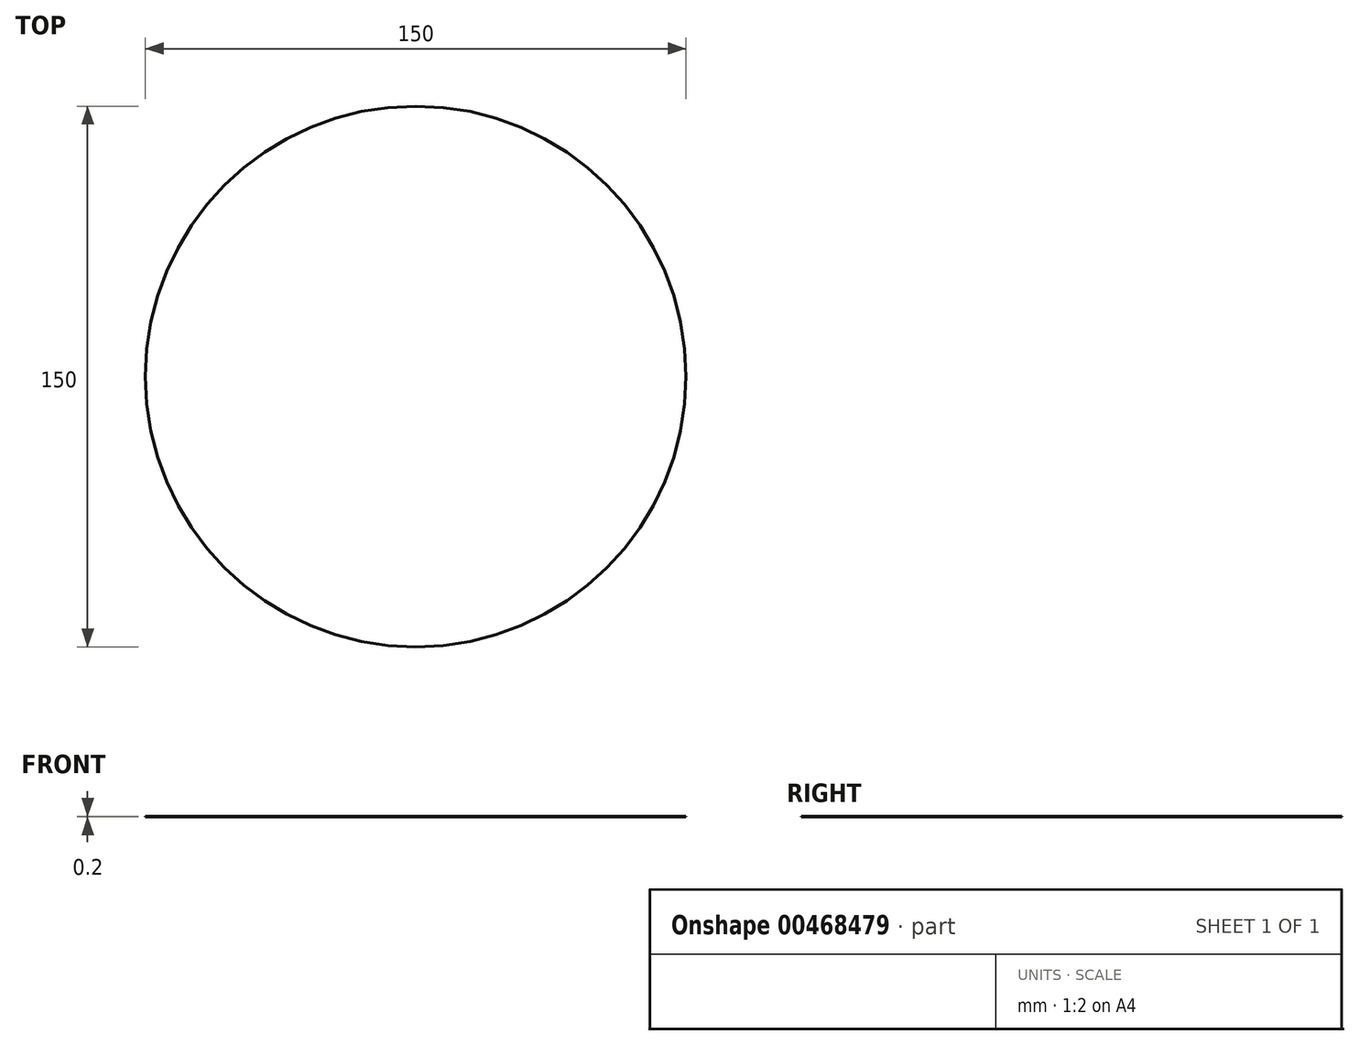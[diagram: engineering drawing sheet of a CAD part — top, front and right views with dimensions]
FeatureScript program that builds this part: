
annotation { "Feature Type Name" : "Feature", "Feature Type Description" : "" }
export const myFeature = defineFeature(function(context is Context, id is Id, definition is map)
    precondition{}
    {
        {
            var Q0;
            Q0=qCreatedBy(makeId("Top.planeOp"),FACE);
            var sketch = newSketch(context, id + "F0", { "sketchPlane" : qUnion([Q0])});
            skCircle(sketch, "E0", {"center": v(0, 0) * mm, "radius": 75 * mm});
            skSolve(sketch);
        }
        {
            var Q0;
            Q0=makeQuery(id+"F0.imprint","IMPRINT",FACE,{"disambiguationData":[TD([[makeQuery(id+"F0.imprint","IMPRINT",EDGE,{"derivedFrom":sQuery(id+"F0.wireOp",EDGE,"E0")}),1.0]])]});
            extrude(context, id + "F1", {"entities" : qUnion([Q0]), "depth" : .2 * mm});
        }
    });
